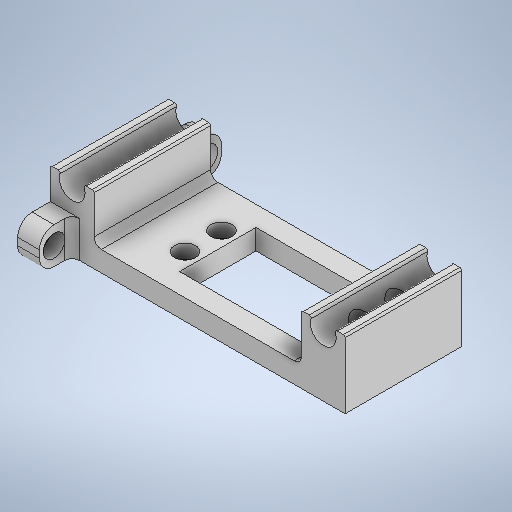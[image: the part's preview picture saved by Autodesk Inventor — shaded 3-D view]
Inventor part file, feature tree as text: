
AUTODESK INVENTOR PART (.ipt)
format: ipt  version: 2025.2 (Build 292293000, 293)  size: 398,336 bytes
history: native  units: mm
features: sketch x5, extrude x4, fillet x4, hole x2
ambient origin geometry x8: Origin, YZ Plane, XZ Plane, XY Plane, X Axis, Y Axis, Z Axis, Center Point
bodies: Solid1 (feature_tree)
feature tree (15):
  extrude  "Base"  Depth=20.0mm
  sketch  "Sketch3"  dims[d4=4.5mm d5=10.0mm d6=4.5mm]
  hole  "Servo mount holes"  [1 undecoded]
  sketch  "Sketch2"  dims[d2=30.0mm d3=10.0mm]
  extrude  "Linear rod mount"  Depth=10.0mm
  extrude  "Servo mount hole extended"  Depth=6.0mm
  fillet  "Fillet1"  Radius=6.0mm
  fillet  "Fillet2"  Radius=5.6mm
  extrude  "Extrusion5"  Depth=0.5mm
  fillet  "Fillet3"  Radius=7.1mm
  hole  "Hole2"  [1 undecoded]
  fillet  "Fillet4"  Radius=10.0mm
  sketch  "Sketch1"  dims[d0=40.0mm d1=20.0mm]
  sketch  "Sketch4"  dims[d7=4.0mm d8=6.0mm d9=6.0mm d10=5.6mm d11=0.0mm]
  sketch  "Sketch5"  dims[d12=12.0mm d13=13.0mm d14=7.1mm d16=3.0mm d17=0.0mm d19=10.0mm d21=4.3mm d22=6.0mm d23=5.8mm d24=4.0mm d25=90.0deg d26=8.0mm d27=20.594885mm d28=5.8mm d29=10.0mm d30=0.0mm d31=0.5mm d32=4.5mm d33=0.5mm d36=2.0mm d37=0.5mm d38=1.8mm d39=10.0mm d40=6.0mm d41=50.0mm d42=0.0mm d43=4.0mm d44=4.5mm d45=6.0mm d46=6.0mm d47=4.0mm d48=90.0deg d49=8.0mm d50=20.594885mm d51=2.0mm d34=0.5mm d35=0.872665mm d52=0.872665mm d53=0.5mm d54=0.872665mm d55=0.872665mm]
note: 2 required parameter values undecoded (feature->parameter linkage not recoverable at this tier; creation-order binding heuristic only, values carry confidence <= 0.55)
